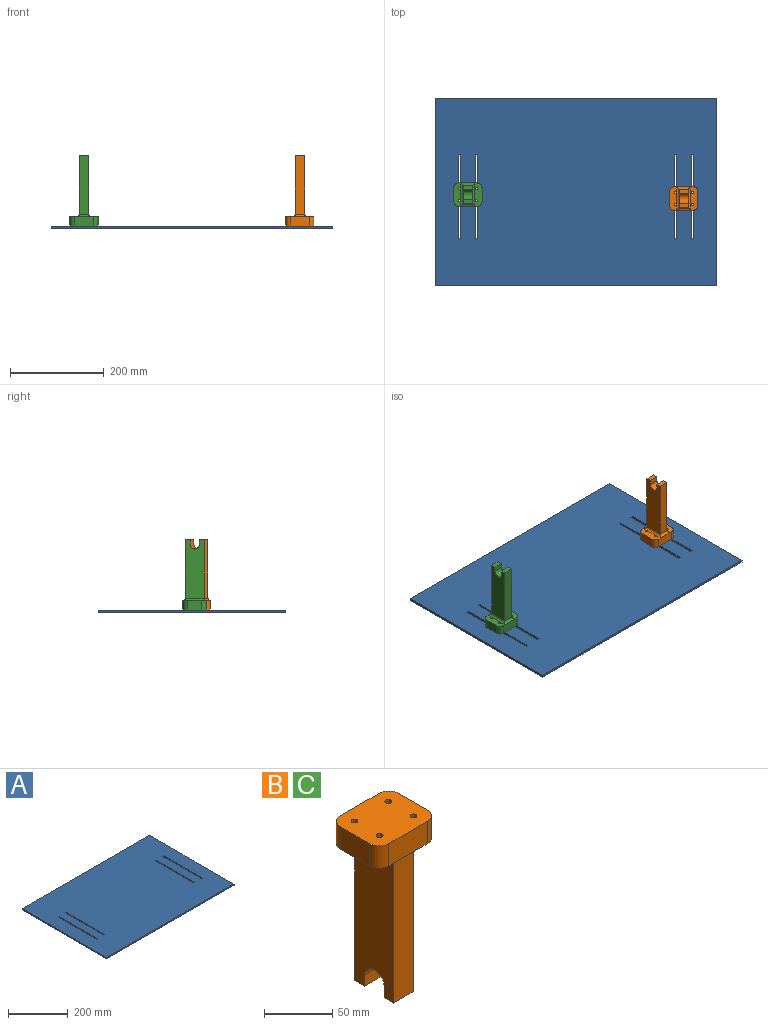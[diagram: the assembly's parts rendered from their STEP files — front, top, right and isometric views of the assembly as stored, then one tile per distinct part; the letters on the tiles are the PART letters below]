
ASSEMBLY  parts=3 mates=2
PART A: 22 faces, bbox 600x400x5 mm
  f0: plane 600x400mm, normal (0,0,1), area 236400mm2, adj f2,f3,f4,f5,f6,f7,f8,f9
  f1: plane 600x400mm, normal (0,0,-1), area 236400mm2, adj f2,f3,f4,f5,f6,f7,f8,f9
  f2: plane 600x5mm, normal (0,1,0), area 3000mm2, adj f0,f1,f3,f5
  f3: plane 400x5mm, normal (-1,0,0), area 2000mm2, adj f0,f1,f2,f4
  f4: plane 600x5mm, normal (0,-1,0), area 3000mm2, adj f0,f1,f3,f5
  f5: plane 400x5mm, normal (1,0,0), area 2000mm2, adj f0,f1,f2,f4
  f6: plane 5x5mm, normal (0,-1,0), area 25mm2, adj f0,f1,f7,f9
  f7: plane 180x5mm, normal (1,0,0), area 900mm2, adj f0,f1,f6,f8
  f8: plane 5x5mm, normal (0,1,0), area 25mm2, adj f0,f1,f7,f9
  f9: plane 180x5mm, normal (-1,0,0), area 900mm2, adj f0,f1,f6,f8
  f10: plane 5x5mm, normal (0,-1,0), area 25mm2, adj f0,f1,f11,f13
  f11: plane 180x5mm, normal (1,0,0), area 900mm2, adj f0,f1,f10,f12
  f12: plane 5x5mm, normal (0,1,0), area 25mm2, adj f0,f1,f11,f13
  f13: plane 180x5mm, normal (-1,0,0), area 900mm2, adj f0,f1,f10,f12
  f14: plane 5x5mm, normal (0,-1,0), area 25mm2, adj f0,f1,f15,f17
  f15: plane 180x5mm, normal (1,0,0), area 900mm2, adj f0,f1,f14,f16
  f16: plane 5x5mm, normal (0,1,0), area 25mm2, adj f0,f1,f15,f17
  f17: plane 180x5mm, normal (-1,0,0), area 900mm2, adj f0,f1,f14,f16
  f18: plane 5x5mm, normal (0,-1,0), area 25mm2, adj f0,f1,f19,f21
  f19: plane 180x5mm, normal (1,0,0), area 900mm2, adj f0,f1,f18,f20
  f20: plane 5x5mm, normal (0,1,0), area 25mm2, adj f0,f1,f19,f21
  f21: plane 180x5mm, normal (-1,0,0), area 900mm2, adj f0,f1,f18,f20
PART B: 28 faces, bbox 60x50x150 mm
  f0: plane 20x10mm, normal (0,0,-1), area 200mm2, adj f1,f2,f14,f26
  f1: plane 125x40mm, normal (-1,0,0), area 4642.9mm2, adj f0,f14,f15,f16,f18,f25,f26,f27
  f2: plane 125x40mm, normal (1,0,0), area 4642.9mm2, adj f0,f14,f15,f16,f19,f25,f26,f27
  f3: plane 50x15mm, normal (0,0,-1), area 667.8mm2, adj f4,f5,f6,f10,f12,f18,f21,f22
  f4: plane 40x20mm, normal (0,1,0), area 800mm2, adj f3,f8,f9,f20,f21,f24
  f5: plane 30x20mm, normal (-1,0,0), area 600mm2, adj f3,f8,f21,f22
  f6: plane 40x20mm, normal (0,-1,0), area 800mm2, adj f3,f8,f9,f17,f22,f23
  f7: plane 30x20mm, normal (1,0,0), area 600mm2, adj f8,f9,f23,f24
  f8: plane 60x50mm, normal (0,0,1), area 2835.6mm2, adj f4,f5,f6,f7,f10,f11,f12,f13
  f9: plane 50x15mm, normal (0,0,-1), area 667.8mm2, adj f4,f6,f7,f11,f13,f19,f23,f24
  f10: cylinder r=2.5mm len=20mm, axis (0,0,-1), area 314.2mm2, adj f3,f8
  f11: cylinder r=2.5mm len=20mm, axis (0,0,-1), area 314.2mm2, adj f8,f9
  f12: cylinder r=2.5mm len=20mm, axis (0,0,-1), area 314.2mm2, adj f3,f8
  f13: cylinder r=2.5mm len=20mm, axis (0,0,-1), area 314.2mm2, adj f8,f9
  f14: plane 125x20mm, normal (0,-1,0), area 2500mm2, adj f0,f1,f2,f17
  f15: plane 125x20mm, normal (0,1,0), area 2500mm2, adj f1,f2,f16,f20
  f16: plane 20x10mm, normal (0,0,-1), area 200mm2, adj f1,f2,f15,f25
  f17: cylinder r=5mm len=30mm, axis (1,0,0), area 185.6mm2, adj f6,f14,f18,f19
  f18: cylinder r=5mm len=50mm, axis (0,-1,0), area 342.7mm2, adj f1,f3,f17,f20
  f19: cylinder r=5mm len=50mm, axis (0,1,0), area 342.7mm2, adj f2,f9,f17,f20
  f20: cylinder r=5mm len=30mm, axis (-1,0,0), area 185.6mm2, adj f4,f15,f18,f19
  f21: cylinder r=10mm len=20mm, axis (0,0,1), area 314.2mm2, adj f3,f4,f5,f8
  f22: cylinder r=10mm len=20mm, axis (0,0,-1), area 314.2mm2, adj f3,f5,f6,f8
  f23: cylinder r=10mm len=20mm, axis (0,0,1), area 314.2mm2, adj f6,f7,f8,f9
  f24: cylinder r=10mm len=20mm, axis (0,0,-1), area 314.2mm2, adj f4,f7,f8,f9
  f25: plane 20x10mm, normal (0,-1,0), area 200mm2, adj f1,f2,f16,f27
  f26: plane 20x10mm, normal (0,1,0), area 200mm2, adj f0,f1,f2,f27
  f27: cylinder r=10mm len=20mm, axis (1,0,0), area 628.3mm2, adj f1,f2,f25,f26
PART C: same geometry as B
PLACE A t=(-40.9,-52.06,-3.36)mm fixed
PLACE B rot(axis=(1,0,0),180deg) t=(914.76,286.09,21.64)mm
PLACE C rot(axis=(1,0,0),180deg) t=(454.81,294.26,21.64)mm
MATE planar A.f0 <-> C.f8  axis (0,0,1) through (-15.18,122.11,1.64)mm
MATE planar B.f8 <-> A.f0  axis (0,0,-1) through (459.62,118.13,1.64)mm
